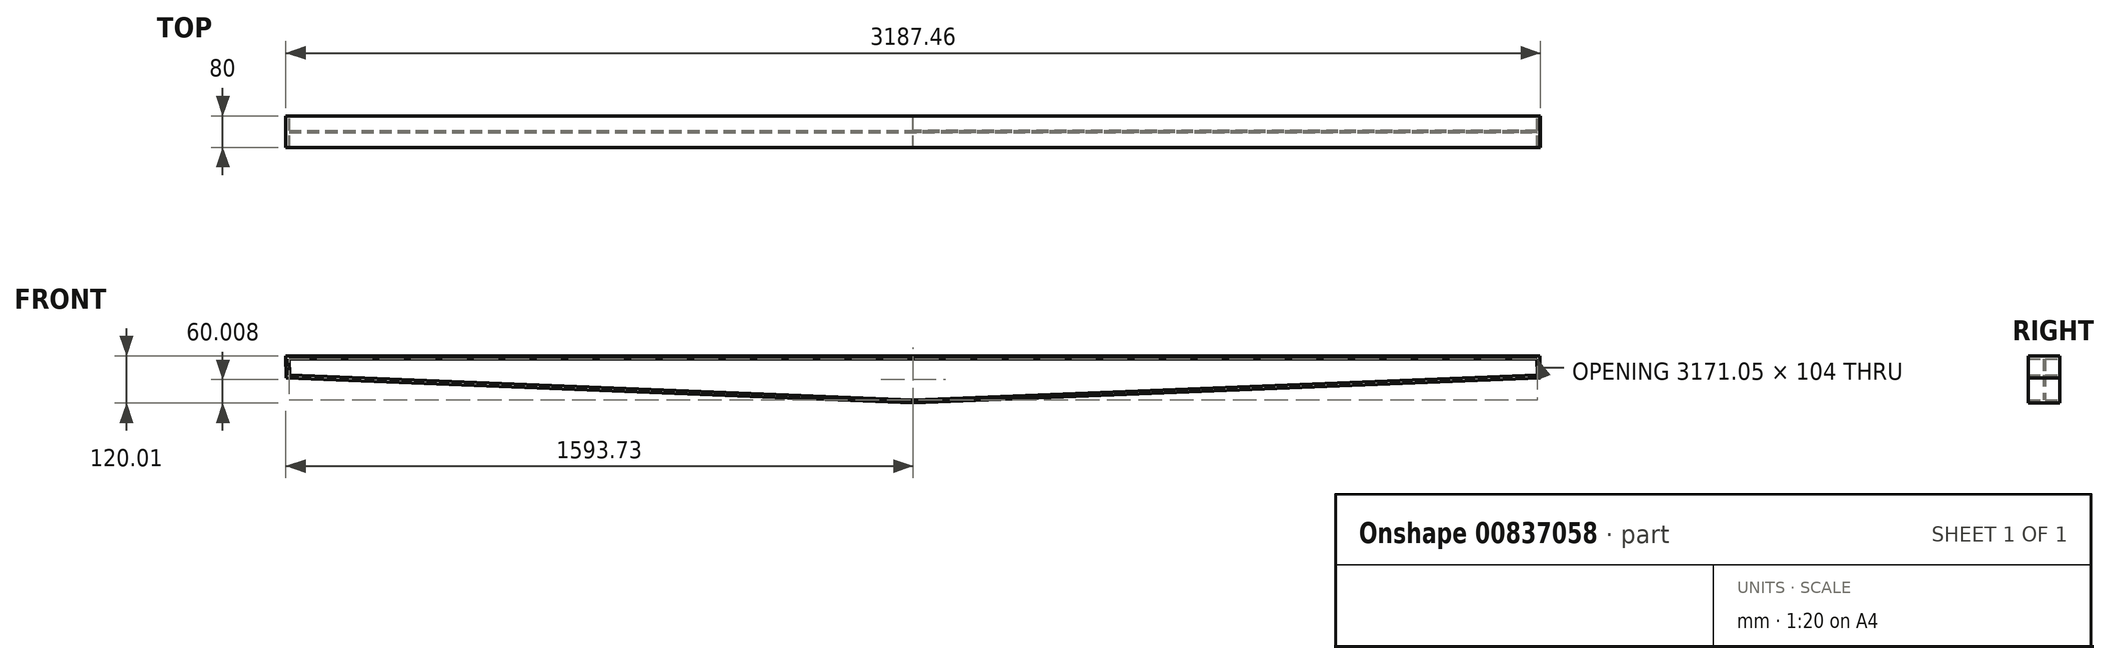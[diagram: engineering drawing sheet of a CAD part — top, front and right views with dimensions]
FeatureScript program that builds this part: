
annotation { "Feature Type Name" : "Feature", "Feature Type Description" : "" }
export const myFeature = defineFeature(function(context is Context, id is Id, definition is map)
    precondition{}
    {
        {
            var Q0;
            Q0=qCreatedBy(makeId("Front.planeOp"),FACE);
            var sketch = newSketch(context, id + "F0", { "sketchPlane" : qUnion([Q0])});
            skLineSegment(sketch, "E0", {"start": v(0, -32.95) * mm, "end": v(-1585, -32.95) * mm});
            skLineSegment(sketch, "E1", {"start": v(-1585, -32.95) * mm, "end": v(-1583.95, -72.94) * mm});
            skLineSegment(sketch, "E2", {"start": v(-1583.95, -72.94) * mm, "end": v(0, -136.95) * mm});
            skLineSegment(sketch, "E3.MirrorCS", {"start": v(0, -32.95) * mm, "end": v(1585, -32.95) * mm});
            skLineSegment(sketch, "E4", {"start": v(1585, -32.95) * mm, "end": v(1586.05, -72.94) * mm});
            skLineSegment(sketch, "E5", {"start": v(1586.05, -72.94) * mm, "end": v(0, -136.95) * mm});
            skSolve(sketch);
        }
        {
            var Q0;
            Q0=qSketchRegion(id+"F0",true);
            extrude(context, id + "F1", {"entities" : qUnion([Q0]), "depth" : 5 * mm, "offsetDistance" : 25 * mm, "symmetric" : true});
        }
        {
            var Q0;
            Q0=qCreatedBy(makeId("Front.planeOp"),FACE);
            var sketch = newSketch(context, id + "F2", { "sketchPlane" : qUnion([Q0])});
            skLineSegment(sketch, "E6", {"start": v(-1585, -32.95) * mm, "end": v(-1583.95, -72.94) * mm});
            skLineSegment(sketch, "E7", {"start": v(-1583.95, -72.94) * mm, "end": v(0, -136.95) * mm});
            skLineSegment(sketch, "E8", {"start": v(0, -136.95) * mm, "end": v(1586.05, -72.94) * mm});
            skLineSegment(sketch, "E9", {"start": v(1586.05, -72.94) * mm, "end": v(1585, -32.95) * mm});
            skLineSegment(sketch, "E10", {"start": v(1585, -32.95) * mm, "end": v(-1585, -32.95) * mm});
            skLineSegment(sketch, "E11", {"start": v(-1593.21, -24.95) * mm, "end": v(-1591.75, -80.63) * mm});
            skLineSegment(sketch, "E12", {"start": v(-1591.75, -80.63) * mm, "end": v(0, -144.96) * mm});
            skLineSegment(sketch, "E13", {"start": v(0, -144.96) * mm, "end": v(1594.25, -80.61) * mm});
            skLineSegment(sketch, "E14", {"start": v(1594.25, -80.61) * mm, "end": v(1592.8, -24.95) * mm});
            skLineSegment(sketch, "E15", {"start": v(1592.8, -24.95) * mm, "end": v(-1593.21, -24.95) * mm});
            skSolve(sketch);
        }
        {
            var Q0;
            Q0=qSketchRegion(id+"F2",true);
            extrude(context, id + "F3", {"entities" : qUnion([Q0]), "operationType" : NewBodyOperationType.ADD, "depth" : 80 * mm, "offsetDistance" : 25 * mm, "symmetric" : true});
        }
    });
